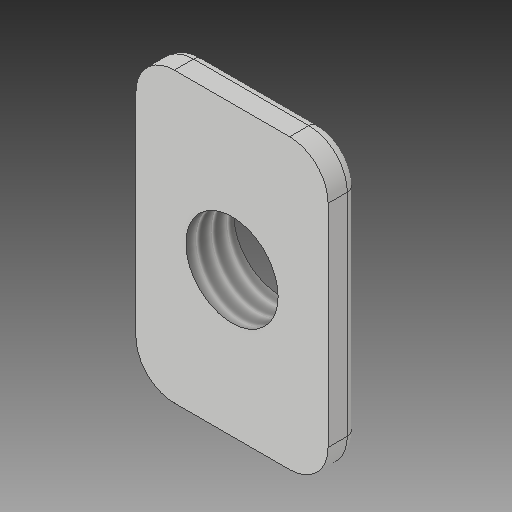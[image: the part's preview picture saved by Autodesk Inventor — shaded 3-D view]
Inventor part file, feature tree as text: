
AUTODESK INVENTOR PART (.ipt)
format: ipt  version: 2018 (Build 220112000, 112)  size: 158,720 bytes
history: native  units: mm
features: other x3, sketch x2
ambient origin geometry x8: Origin, YZ Plane, XZ Plane, XY Plane, X Axis, Y Axis, Z Axis, Center Point
bodies: Solid1 (feature_tree)
feature tree (5):
  other  "M5 Tee Nut-Generic_MIR_MIR.ipt"
  other  "Solid1::M5 Tee Nut-Generic_MIR_MIR.ipt"
  other  "TaggingFeature1"
  sketch  "Sketch1"  dims[d0=10.0mm]
  sketch  "Sketch2"
